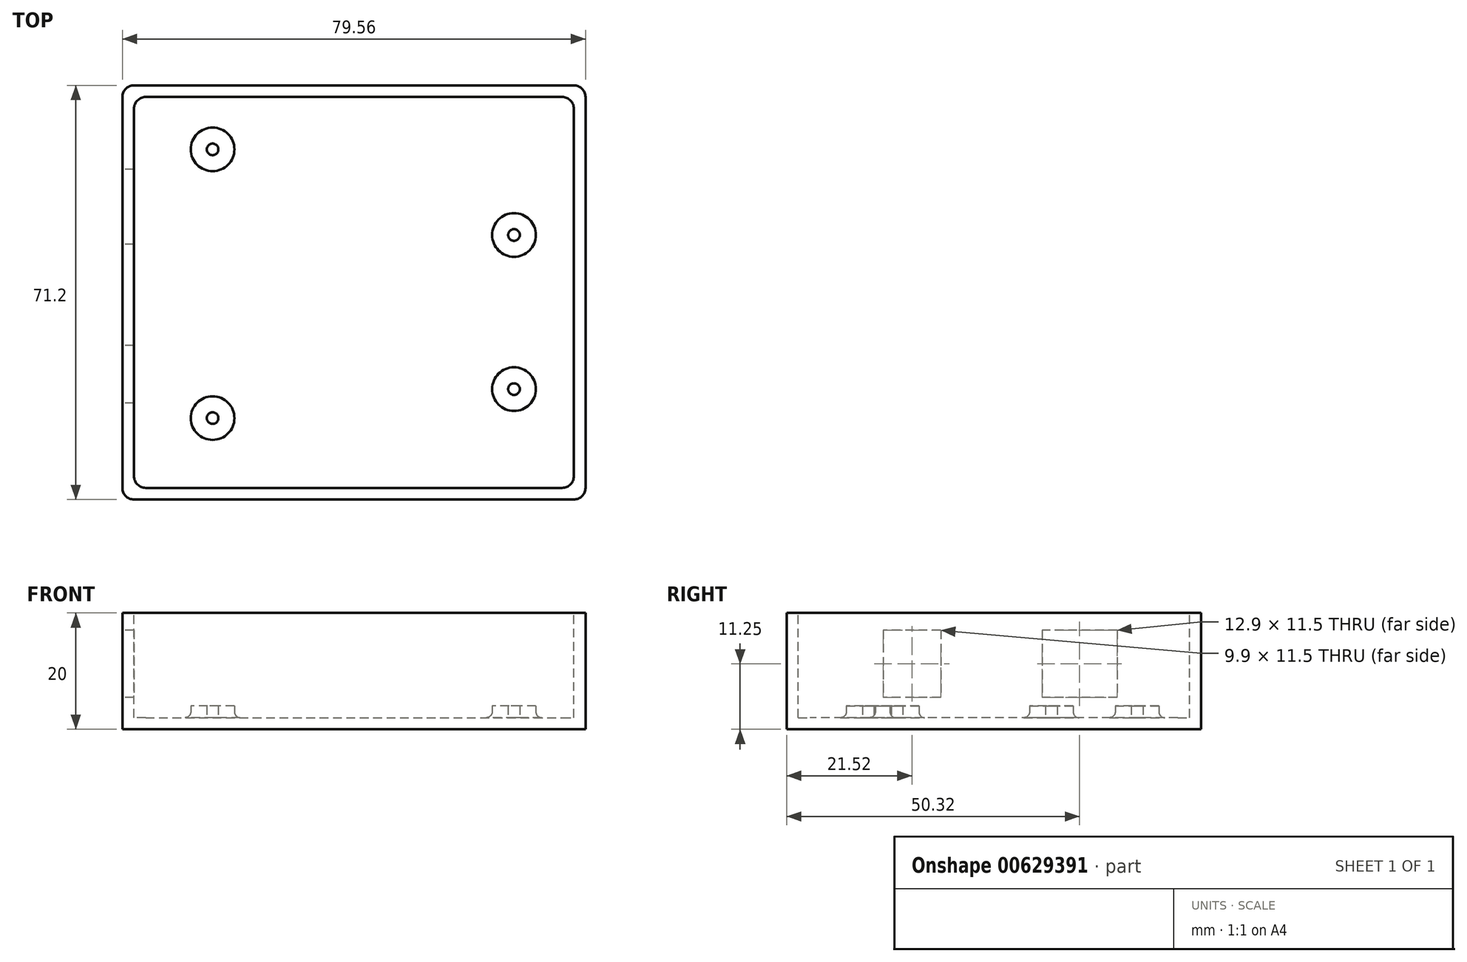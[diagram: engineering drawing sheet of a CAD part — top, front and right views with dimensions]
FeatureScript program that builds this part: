
annotation { "Feature Type Name" : "Feature", "Feature Type Description" : "" }
export const myFeature = defineFeature(function(context is Context, id is Id, definition is map)
    precondition{}
    {
        {
            var Q0;
            Q0=qCreatedBy(makeId("Top.planeOp"),FACE);
            var sketch = newSketch(context, id + "F0", { "sketchPlane" : qUnion([Q0])});
            skLineSegment(sketch, "E0.bottom", {"start": v(-39.78, 35.6) * mm, "end": v(39.78, 35.6) * mm});
            skLineSegment(sketch, "E0.top", {"start": v(-39.78, -35.6) * mm, "end": v(39.78, -35.6) * mm});
            skLineSegment(sketch, "E0.left", {"start": v(-39.78, 35.6) * mm, "end": v(-39.78, -35.6) * mm});
            skLineSegment(sketch, "E0.right", {"start": v(39.78, 35.6) * mm, "end": v(39.78, -35.6) * mm});
            skPoint(sketch, "E0.middle", {"position": v(0, 0) * mm});
            skSolve(sketch);
        }
        {
            var Q0;
            Q0 = qSketchRegion(id + "F0", true);
            extrude(context, id + "F1", {"entities" : qUnion([Q0]), "depth" : 20 * mm, "offsetDistance" : 25 * mm});
        }
        {
            var Q0;
            Q0=makeQuery(id+"F1.opExtrude","CAP_FACE",FACE,{"disambiguationData":[OSD([sQuery(id+"F0.wireOp",EDGE,"E0.bottom"),sQuery(id+"F0.wireOp",EDGE,"E0.top"),sQuery(id+"F0.wireOp",EDGE,"E0.left"),sQuery(id+"F0.wireOp",EDGE,"E0.right")])],"isStart":false});
            var sketch = newSketch(context, id + "F2", { "sketchPlane" : qUnion([Q0])});
            skSolve(sketch);
        }
        {
            var Q0;
            Q0=makeQuery(id+"F1.opExtrude","SWEPT_EDGE",EDGE,{"disambiguationData":[OSD([sQuery(id+"F0.wireOp",EDGE,"E0.top"),sQuery(id+"F0.wireOp",EDGE,"E0.right")])]});
            var Q1;
            Q1=makeQuery(id+"F1.opExtrude","SWEPT_EDGE",EDGE,{"disambiguationData":[OSD([sQuery(id+"F0.wireOp",EDGE,"E0.bottom"),sQuery(id+"F0.wireOp",EDGE,"E0.right")])]});
            var Q2;
            Q2=makeQuery(id+"F1.opExtrude","SWEPT_EDGE",EDGE,{"disambiguationData":[OSD([sQuery(id+"F0.wireOp",EDGE,"E0.bottom"),sQuery(id+"F0.wireOp",EDGE,"E0.left")])]});
            var Q3;
            Q3=makeQuery(id+"F1.opExtrude","SWEPT_EDGE",EDGE,{"disambiguationData":[OSD([sQuery(id+"F0.wireOp",EDGE,"E0.top"),sQuery(id+"F0.wireOp",EDGE,"E0.left")])]});
            fillet(context, id + "F3", {"entities" : qUnion([Q0, Q1, Q2, Q3]), "radius" : 2 * mm, "tangentPropagation" : true, "allowEdgeOverflow" : false});
        }
        {
            var Q0;
            Q0=makeQuery(id+"F2.imprint","IMPRINT",FACE,{"disambiguationData":[TD([[makeQuery(id+"F2.imprint","IMPRINT",EDGE,{"derivedFrom":makeQuery(id+"F1.opExtrude","CAP_EDGE",EDGE,{"disambiguationData":[OSD([sQuery(id+"F0.wireOp",EDGE,"E0.bottom")])],"isStart":false})}),-1.0]])]});
            var sketch = newSketch(context, id + "F4", { "sketchPlane" : qUnion([Q0])});
            skLineSegment(sketch, "E1.bottom", {"start": v(-35.78, 33.6) * mm, "end": v(35.78, 33.6) * mm});
            skLineSegment(sketch, "E1.top", {"start": v(-35.78, -33.6) * mm, "end": v(35.78, -33.6) * mm});
            skLineSegment(sketch, "E1.left", {"start": v(-37.78, 31.6) * mm, "end": v(-37.78, -31.6) * mm});
            skLineSegment(sketch, "E1.right", {"start": v(37.78, 31.6) * mm, "end": v(37.78, -31.6) * mm});
            skPoint(sketch, "E1.middle", {"position": v(0, 0) * mm});
            skPoint(sketch, "E2.visualSharp", {"position": v(-37.78, 33.6) * mm});
            skArc(sketch, "E2.filletArc", {"start": v(-35.78, 33.6) * mm, "mid": v(-37.2, 33.01) * mm, "end": v(-37.78, 31.6) * mm});
            skPoint(sketch, "E3.visualSharp", {"position": v(37.78, 33.6) * mm});
            skArc(sketch, "E3.filletArc", {"start": v(37.78, 31.6) * mm, "mid": v(37.2, 33.01) * mm, "end": v(35.78, 33.6) * mm});
            skPoint(sketch, "E4.visualSharp", {"position": v(-37.78, -33.6) * mm});
            skArc(sketch, "E4.filletArc", {"start": v(-37.78, -31.6) * mm, "mid": v(-37.2, -33.01) * mm, "end": v(-35.78, -33.6) * mm});
            skPoint(sketch, "E5.visualSharp", {"position": v(37.78, -33.6) * mm});
            skArc(sketch, "E5.filletArc", {"start": v(35.78, -33.6) * mm, "mid": v(37.2, -33.01) * mm, "end": v(37.78, -31.6) * mm});
            skSolve(sketch);
        }
        {
            var Q0;
            Q0=makeQuery(id+"F1.opExtrude","CAP_FACE",FACE,{"disambiguationData":[OSD([sQuery(id+"F0.wireOp",EDGE,"E0.bottom"),sQuery(id+"F0.wireOp",EDGE,"E0.top"),sQuery(id+"F0.wireOp",EDGE,"E0.left"),sQuery(id+"F0.wireOp",EDGE,"E0.right")])],"isStart":false});
            shell(context, id + "F5", {"entities" : qUnion([Q0]), "thickness" : 2 * mm});
        }
        {
            var Q0;
            Q0=makeQuery(id+"F5.opShell","OFFSET_EDGE",EDGE,{"disambiguationData":[OSD([sQuery(id+"F0.wireOp",EDGE,"E0.bottom"),sQuery(id+"F0.wireOp",EDGE,"E0.left")])]});
            var Q1;
            Q1=makeQuery(id+"F5.opShell","OFFSET_EDGE",EDGE,{"disambiguationData":[OSD([sQuery(id+"F0.wireOp",EDGE,"E0.bottom"),sQuery(id+"F0.wireOp",EDGE,"E0.right")])]});
            var Q2;
            Q2=makeQuery(id+"F5.opShell","OFFSET_EDGE",EDGE,{"disambiguationData":[OSD([sQuery(id+"F0.wireOp",EDGE,"E0.top"),sQuery(id+"F0.wireOp",EDGE,"E0.left")])]});
            var Q3;
            Q3=makeQuery(id+"F5.opShell","OFFSET_EDGE",EDGE,{"disambiguationData":[OSD([sQuery(id+"F0.wireOp",EDGE,"E0.top"),sQuery(id+"F0.wireOp",EDGE,"E0.right")])]});
            fillet(context, id + "F6", {"entities" : qUnion([Q0, Q1, Q2, Q3]), "radius" : 2 * mm, "tangentPropagation" : true, "allowEdgeOverflow" : false});
        }
        {
            var Q0;
            Q0=makeQuery(id+"F1.opExtrude","SWEPT_FACE",FACE,{"disambiguationData":[OSD([sQuery(id+"F0.wireOp",EDGE,"E0.left")])]});
            var sketch = newSketch(context, id + "F7", { "sketchPlane" : qUnion([Q0])});
            skLineSegment(sketch, "E6.bottom", {"start": v(-21.17, 17) * mm, "end": v(-8.27, 17) * mm});
            skLineSegment(sketch, "E6.top", {"start": v(-21.17, 5.5) * mm, "end": v(-8.27, 5.5) * mm});
            skLineSegment(sketch, "E6.left", {"start": v(-21.17, 17) * mm, "end": v(-21.17, 5.5) * mm});
            skLineSegment(sketch, "E6.right", {"start": v(-8.27, 17) * mm, "end": v(-8.27, 5.5) * mm});
            skSolve(sketch);
        }
        {
            var Q0;
            Q0 = qSketchRegion(id + "F7", true);
            extrude(context, id + "F8", {"entities" : qUnion([Q0]), "operationType" : NewBodyOperationType.REMOVE, "oppositeDirection" : true, "depth" : 2 * mm, "offsetDistance" : 25 * mm});
        }
        {
            var Q0;
            Q0=makeQuery(id+"F1.opExtrude","SWEPT_FACE",FACE,{"disambiguationData":[OSD([sQuery(id+"F0.wireOp",EDGE,"E0.left")])]});
            var sketch = newSketch(context, id + "F9", { "sketchPlane" : qUnion([Q0])});
            skLineSegment(sketch, "E7.bottom", {"start": v(9.13, 17) * mm, "end": v(19.03, 17) * mm});
            skLineSegment(sketch, "E7.top", {"start": v(9.13, 5.5) * mm, "end": v(19.03, 5.5) * mm});
            skLineSegment(sketch, "E7.left", {"start": v(9.13, 17) * mm, "end": v(9.13, 5.5) * mm});
            skLineSegment(sketch, "E7.right", {"start": v(19.03, 17) * mm, "end": v(19.03, 5.5) * mm});
            skSolve(sketch);
        }
        {
            var Q0;
            Q0 = qSketchRegion(id + "F9", true);
            extrude(context, id + "F10", {"entities" : qUnion([Q0]), "operationType" : NewBodyOperationType.REMOVE, "oppositeDirection" : true, "depth" : 2 * mm, "offsetDistance" : 25 * mm});
        }
        {
            var Q0;
            Q0=qCreatedBy(makeId("Top.planeOp"),FACE);
            var sketch = newSketch(context, id + "F11", { "sketchPlane" : qUnion([Q0])});
            skCircle(sketch, "E8", {"center": v(-24.28, 24.6) * mm, "radius": 3.75 * mm});
            skCircle(sketch, "E9", {"center": v(27.5, 9.88) * mm, "radius": 3.75 * mm});
            skCircle(sketch, "E10", {"center": v(-24.28, -21.6) * mm, "radius": 3.75 * mm});
            skCircle(sketch, "E11", {"center": v(27.5, -16.62) * mm, "radius": 3.75 * mm});
            skCircle(sketch, "E12", {"center": v(27.5, 9.88) * mm, "radius": 1 * mm});
            skCircle(sketch, "E13", {"center": v(-24.28, 24.6) * mm, "radius": 1 * mm});
            skCircle(sketch, "E14", {"center": v(-24.28, -21.6) * mm, "radius": 1 * mm});
            skCircle(sketch, "E15", {"center": v(27.5, -16.62) * mm, "radius": 1 * mm});
            skSolve(sketch);
        }
        {
            var Q0;
            Q0 = qSketchRegion(id + "F11", true);
            extrude(context, id + "F12", {"entities" : qUnion([Q0]), "operationType" : NewBodyOperationType.ADD, "depth" : 4 * mm, "offsetDistance" : 25 * mm});
        }
        {
            var Q0;
            Q0=makeQuery(id+"F12.boolean.opBoolean","INTERSECT",EDGE,{"derivedFrom":[makeQuery(id+"F5.opShell","OFFSET_FACE",FACE,{"disambiguationData":[OSD([sQuery(id+"F0.wireOp",EDGE,"E0.bottom"),sQuery(id+"F0.wireOp",EDGE,"E0.top"),sQuery(id+"F0.wireOp",EDGE,"E0.left"),sQuery(id+"F0.wireOp",EDGE,"E0.right")])]}),makeQuery(id+"F12.opExtrude","SWEPT_FACE",FACE,{"disambiguationData":[OSD([sQuery(id+"F11.wireOp",EDGE,"E8")])]})]});
            var Q1;
            Q1=makeQuery(id+"F12.boolean.opBoolean","INTERSECT",EDGE,{"derivedFrom":[makeQuery(id+"F5.opShell","OFFSET_FACE",FACE,{"disambiguationData":[OSD([sQuery(id+"F0.wireOp",EDGE,"E0.bottom"),sQuery(id+"F0.wireOp",EDGE,"E0.top"),sQuery(id+"F0.wireOp",EDGE,"E0.left"),sQuery(id+"F0.wireOp",EDGE,"E0.right")])]}),makeQuery(id+"F12.opExtrude","SWEPT_FACE",FACE,{"disambiguationData":[OSD([sQuery(id+"F11.wireOp",EDGE,"E10")])]})]});
            var Q2;
            Q2=makeQuery(id+"F12.boolean.opBoolean","INTERSECT",EDGE,{"derivedFrom":[makeQuery(id+"F5.opShell","OFFSET_FACE",FACE,{"disambiguationData":[OSD([sQuery(id+"F0.wireOp",EDGE,"E0.bottom"),sQuery(id+"F0.wireOp",EDGE,"E0.top"),sQuery(id+"F0.wireOp",EDGE,"E0.left"),sQuery(id+"F0.wireOp",EDGE,"E0.right")])]}),makeQuery(id+"F12.opExtrude","SWEPT_FACE",FACE,{"disambiguationData":[OSD([sQuery(id+"F11.wireOp",EDGE,"E9")])]})]});
            var Q3;
            Q3=makeQuery(id+"F12.boolean.opBoolean","INTERSECT",EDGE,{"derivedFrom":[makeQuery(id+"F5.opShell","OFFSET_FACE",FACE,{"disambiguationData":[OSD([sQuery(id+"F0.wireOp",EDGE,"E0.bottom"),sQuery(id+"F0.wireOp",EDGE,"E0.top"),sQuery(id+"F0.wireOp",EDGE,"E0.left"),sQuery(id+"F0.wireOp",EDGE,"E0.right")])]}),makeQuery(id+"F12.opExtrude","SWEPT_FACE",FACE,{"disambiguationData":[OSD([sQuery(id+"F11.wireOp",EDGE,"E11")])]})]});
            fillet(context, id + "F13", {"entities" : qUnion([Q0, Q1, Q2, Q3]), "radius" : 1 * mm, "tangentPropagation" : true, "allowEdgeOverflow" : false});
        }
    });
